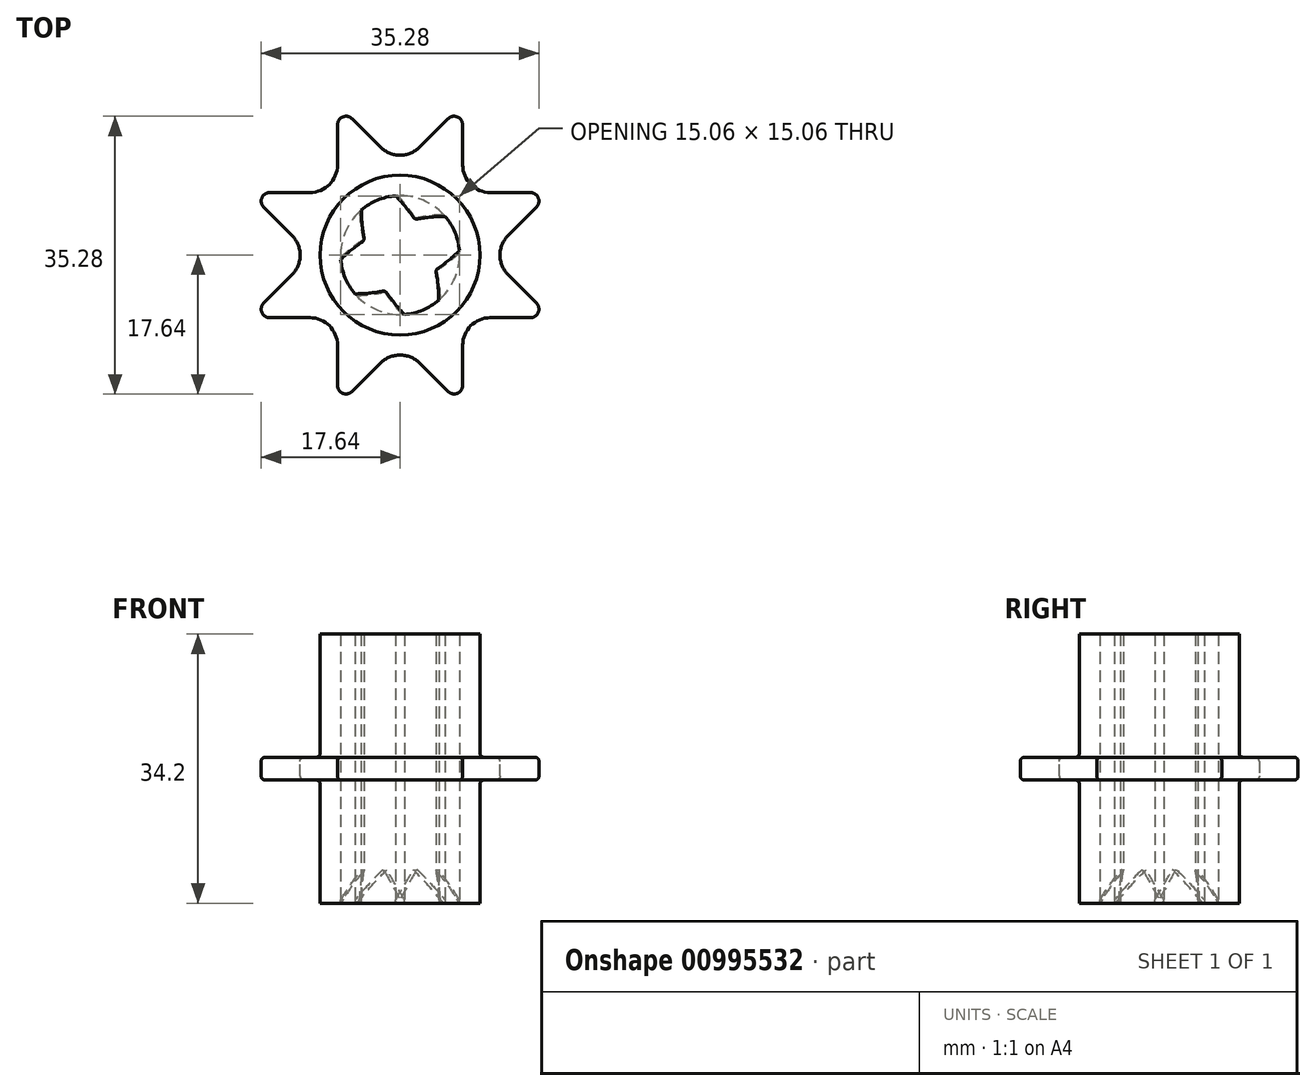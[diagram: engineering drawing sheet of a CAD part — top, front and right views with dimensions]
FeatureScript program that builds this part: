
annotation { "Feature Type Name" : "Feature", "Feature Type Description" : "" }
export const myFeature = defineFeature(function(context is Context, id is Id, definition is map)
    precondition{}
    {
        {
            var Q0;
            Q0=qCreatedBy(makeId("Top.planeOp"),FACE);
            var sketch = newSketch(context, id + "F0", { "sketchPlane" : qUnion([Q0])});
            skCircle(sketch, "E0", {"center": v(0, 0) * mm, "radius": 7.95 * mm, "construction": true});
            skCircle(sketch, "E1", {"center": v(0, 0) * mm, "radius": 20.77 * mm, "construction": true});
            skLineSegment(sketch, "E2", {"start": v(-19.2, 7.95) * mm, "end": v(19.2, 7.95) * mm, "construction": true});
            skLineSegment(sketch, "E3", {"start": v(-19.2, -7.95) * mm, "end": v(19.2, -7.95) * mm, "construction": true});
            skLineSegment(sketch, "E4", {"start": v(-7.95, -19.2) * mm, "end": v(-7.95, 19.2) * mm, "construction": true});
            skLineSegment(sketch, "E5", {"start": v(7.95, 19.2) * mm, "end": v(7.95, -19.2) * mm, "construction": true});
            skLineSegment(sketch, "E6", {"start": v(-19.2, -7.95) * mm, "end": v(7.95, 19.2) * mm, "construction": true});
            skLineSegment(sketch, "E7", {"start": v(-7.95, 19.2) * mm, "end": v(19.2, -7.95) * mm, "construction": true});
            skLineSegment(sketch, "E8", {"start": v(-7.95, -19.2) * mm, "end": v(19.2, 7.95) * mm, "construction": true});
            skLineSegment(sketch, "E9", {"start": v(7.95, -19.2) * mm, "end": v(-19.2, 7.95) * mm, "construction": true});
            skLineSegment(sketch, "E10", {"start": v(-7.95, -19.2) * mm, "end": v(0, -11.24) * mm});
            skLineSegment(sketch, "E11", {"start": v(0, -11.24) * mm, "end": v(7.95, -19.2) * mm});
            skLineSegment(sketch, "E12", {"start": v(7.95, -7.95) * mm, "end": v(7.95, -19.2) * mm});
            skLineSegment(sketch, "E13", {"start": v(19.2, -7.95) * mm, "end": v(7.95, -7.95) * mm});
            skLineSegment(sketch, "E14", {"start": v(11.24, 0) * mm, "end": v(19.2, -7.95) * mm});
            skLineSegment(sketch, "E15", {"start": v(19.2, 7.95) * mm, "end": v(11.24, 0) * mm});
            skLineSegment(sketch, "E16", {"start": v(19.2, 7.95) * mm, "end": v(7.95, 7.95) * mm});
            skLineSegment(sketch, "E17", {"start": v(7.95, 7.95) * mm, "end": v(7.95, 19.2) * mm});
            skLineSegment(sketch, "E18", {"start": v(7.95, 19.2) * mm, "end": v(0, 11.24) * mm});
            skLineSegment(sketch, "E19", {"start": v(-7.95, 19.2) * mm, "end": v(0, 11.24) * mm});
            skLineSegment(sketch, "E20", {"start": v(-7.95, 19.2) * mm, "end": v(-7.95, 7.95) * mm});
            skLineSegment(sketch, "E21", {"start": v(-7.95, 7.95) * mm, "end": v(-19.2, 7.95) * mm});
            skLineSegment(sketch, "E22", {"start": v(-19.2, 7.95) * mm, "end": v(-11.24, 0) * mm});
            skLineSegment(sketch, "E23", {"start": v(-11.24, 0) * mm, "end": v(-19.2, -7.95) * mm});
            skLineSegment(sketch, "E24", {"start": v(-19.2, -7.95) * mm, "end": v(-7.95, -7.95) * mm});
            skLineSegment(sketch, "E25", {"start": v(-7.95, -7.95) * mm, "end": v(-7.95, -19.2) * mm});
            skCircle(sketch, "E26", {"center": v(0, 0) * mm, "radius": 10.15 * mm});
            skSolve(sketch);
        }
        {
            var Q0;
            Q0=makeQuery(id+"F0.imprint","IMPRINT",FACE,{"disambiguationData":[TD([[makeQuery(id+"F0.imprint","IMPRINT",EDGE,{"derivedFrom":sQuery(id+"F0.wireOp",EDGE,"E26")}),1.0]])]});
            extrude(context, id + "F1", {"entities" : qUnion([Q0]), "endBound" : BoundingType.SYMMETRIC, "depth" : 34.2 * mm, "offsetDistance" : 25 * mm});
        }
        {
            var Q0;
            Q0=makeQuery(id+"F0.imprint","IMPRINT",FACE,{"disambiguationData":[TD([[makeQuery(id+"F0.imprint","IMPRINT",EDGE,{"derivedFrom":sQuery(id+"F0.wireOp",EDGE,"E10")}),1.0]])]});
            var Q1;
            Q1=makeQuery(id+"F0.imprint","IMPRINT",FACE,{"disambiguationData":[TD([[makeQuery(id+"F0.imprint","IMPRINT",EDGE,{"derivedFrom":sQuery(id+"F0.wireOp",EDGE,"E26")}),1.0]])]});
            extrude(context, id + "F2", {"entities" : qUnion([Q0, Q1]), "operationType" : NewBodyOperationType.ADD, "endBound" : BoundingType.SYMMETRIC, "depth" : 2.9 * mm, "offsetDistance" : 25 * mm});
        }
        {
            var Q0;
            Q0=makeQuery(id+"F2.opExtrude","SWEPT_EDGE",EDGE,{"disambiguationData":[OSD([sQuery(id+"F0.wireOp",EDGE,"E16"),sQuery(id+"F0.wireOp",EDGE,"E17")])]});
            var Q1;
            Q1=makeQuery(id+"F2.opExtrude","SWEPT_EDGE",EDGE,{"disambiguationData":[OSD([sQuery(id+"F0.wireOp",EDGE,"E18"),sQuery(id+"F0.wireOp",EDGE,"E19")])]});
            var Q2;
            Q2=makeQuery(id+"F2.opExtrude","SWEPT_EDGE",EDGE,{"disambiguationData":[OSD([sQuery(id+"F0.wireOp",EDGE,"E20"),sQuery(id+"F0.wireOp",EDGE,"E21")])]});
            var Q3;
            Q3=makeQuery(id+"F2.opExtrude","SWEPT_EDGE",EDGE,{"disambiguationData":[OSD([sQuery(id+"F0.wireOp",EDGE,"E22"),sQuery(id+"F0.wireOp",EDGE,"E23")])]});
            var Q4;
            Q4=makeQuery(id+"F2.opExtrude","SWEPT_EDGE",EDGE,{"disambiguationData":[OSD([sQuery(id+"F0.wireOp",EDGE,"E24"),sQuery(id+"F0.wireOp",EDGE,"E25")])]});
            var Q5;
            Q5=makeQuery(id+"F2.opExtrude","SWEPT_EDGE",EDGE,{"disambiguationData":[OSD([sQuery(id+"F0.wireOp",EDGE,"E10"),sQuery(id+"F0.wireOp",EDGE,"E11")])]});
            var Q6;
            Q6=makeQuery(id+"F2.opExtrude","SWEPT_EDGE",EDGE,{"disambiguationData":[OSD([sQuery(id+"F0.wireOp",EDGE,"E12"),sQuery(id+"F0.wireOp",EDGE,"E13")])]});
            var Q7;
            Q7=makeQuery(id+"F2.opExtrude","SWEPT_EDGE",EDGE,{"disambiguationData":[OSD([sQuery(id+"F0.wireOp",EDGE,"E14"),sQuery(id+"F0.wireOp",EDGE,"E15")])]});
            fillet(context, id + "F3", {"entities" : qUnion([Q0, Q1, Q2, Q3, Q4, Q5, Q6, Q7]), "radius" : 3.5 * mm, "tangentPropagation" : true, "allowEdgeOverflow" : false});
        }
        {
            var Q0;
            Q0=makeQuery(id+"F2.opExtrude","SWEPT_EDGE",EDGE,{"disambiguationData":[OSD([sQuery(id+"F0.wireOp",EDGE,"E13"),sQuery(id+"F0.wireOp",EDGE,"E14")])]});
            var Q1;
            Q1=makeQuery(id+"F2.opExtrude","SWEPT_EDGE",EDGE,{"disambiguationData":[OSD([sQuery(id+"F0.wireOp",EDGE,"E11"),sQuery(id+"F0.wireOp",EDGE,"E12")])]});
            var Q2;
            Q2=makeQuery(id+"F2.opExtrude","SWEPT_EDGE",EDGE,{"disambiguationData":[OSD([sQuery(id+"F0.wireOp",EDGE,"E10"),sQuery(id+"F0.wireOp",EDGE,"E25")])]});
            var Q3;
            Q3=makeQuery(id+"F2.opExtrude","SWEPT_EDGE",EDGE,{"disambiguationData":[OSD([sQuery(id+"F0.wireOp",EDGE,"E23"),sQuery(id+"F0.wireOp",EDGE,"E24")])]});
            var Q4;
            Q4=makeQuery(id+"F2.opExtrude","SWEPT_EDGE",EDGE,{"disambiguationData":[OSD([sQuery(id+"F0.wireOp",EDGE,"E21"),sQuery(id+"F0.wireOp",EDGE,"E22")])]});
            var Q5;
            Q5=makeQuery(id+"F2.opExtrude","SWEPT_EDGE",EDGE,{"disambiguationData":[OSD([sQuery(id+"F0.wireOp",EDGE,"E19"),sQuery(id+"F0.wireOp",EDGE,"E20")])]});
            var Q6;
            Q6=makeQuery(id+"F2.opExtrude","SWEPT_EDGE",EDGE,{"disambiguationData":[OSD([sQuery(id+"F0.wireOp",EDGE,"E17"),sQuery(id+"F0.wireOp",EDGE,"E18")])]});
            var Q7;
            Q7=makeQuery(id+"F2.opExtrude","SWEPT_EDGE",EDGE,{"disambiguationData":[OSD([sQuery(id+"F0.wireOp",EDGE,"E15"),sQuery(id+"F0.wireOp",EDGE,"E16")])]});
            fillet(context, id + "F4", {"entities" : qUnion([Q0, Q1, Q2, Q3, Q4, Q5, Q6, Q7]), "radius" : 1.1 * mm, "tangentPropagation" : true, "allowEdgeOverflow" : false});
        }
        {
            var Q0;
            Q0=makeQuery(id+"F1.opExtrude","CAP_FACE",FACE,{"disambiguationData":[OSD([sQuery(id+"F0.wireOp",EDGE,"E26")])],"isStart":true});
            var sketch = newSketch(context, id + "F5", { "sketchPlane" : qUnion([Q0])});
            skCircle(sketch, "E27", {"center": v(0, 0) * mm, "radius": 7.55 * mm});
            skCircle(sketch, "E28.0", {"center": v(0, 0) * mm, "radius": 10.15 * mm});
            skArc(sketch, "E29.0", {"start": v(7.95, 16.54) * mm, "mid": v(7.27, 17.55) * mm, "end": v(6.07, 17.32) * mm});
            skArc(sketch, "E29.1", {"start": v(-7.95, -16.54) * mm, "mid": v(-7.27, -17.55) * mm, "end": v(-6.07, -17.32) * mm});
            skLineSegment(sketch, "E30", {"start": v(6.85, 16.54) * mm, "end": v(-6.85, -16.54) * mm, "construction": true});
            skLineSegment(sketch, "E31", {"start": v(-4.92, -5.73) * mm, "end": v(0.57, 7.53) * mm, "construction": true});
            skLineSegment(sketch, "E32", {"start": v(-0.57, -7.53) * mm, "end": v(4.92, 5.73) * mm, "construction": true});
            skLineSegment(sketch, "E33", {"start": v(-7.53, 0.57) * mm, "end": v(5.73, -4.92) * mm, "construction": true});
            skPoint(sketch, "E34.endSnap0", {"position": v(2.18, -0.9) * mm});
            skLineSegment(sketch, "E35", {"start": v(-5.73, 4.92) * mm, "end": v(7.53, -0.57) * mm, "construction": true});
            skLineSegment(sketch, "E36", {"start": v(0, 0) * mm, "end": v(8.18, -3.39) * mm, "construction": true});
            skArc(sketch, "E37", {"start": v(0.57, 7.53) * mm, "mid": v(-3.5, 1.45) * mm, "end": v(-4.92, -5.73) * mm});
            skArc(sketch, "E38", {"start": v(-0.57, -7.53) * mm, "mid": v(3.5, -1.45) * mm, "end": v(4.92, 5.73) * mm});
            skArc(sketch, "E39", {"start": v(7.53, -0.57) * mm, "mid": v(1.45, 3.5) * mm, "end": v(-5.73, 4.92) * mm});
            skArc(sketch, "E40", {"start": v(-7.53, 0.57) * mm, "mid": v(-1.45, -3.5) * mm, "end": v(5.73, -4.92) * mm});
            skPoint(sketch, "E41", {"position": v(1.87, -4.52) * mm});
            skPoint(sketch, "E42", {"position": v(4.52, 1.87) * mm});
            skSolve(sketch);
        }
        {
            var Q0;
            {var subQ0=sQuery(id+"F5.wireOp",EDGE,"E37");var subQ1=sQuery(id+"F5.wireOp",EDGE,"E27");var subQ2=makeQuery(id+"F5.imprint","INTERSECT",VERTEX,{"disambiguationData":[OD(0.0)],"derivedFrom":[subQ1,subQ0]});Q0=makeQuery(id+"F5.imprint","IMPRINT",FACE,{"disambiguationData":[TD([[makeQuery(id+"F5.imprint","IMPRINT",EDGE,{"disambiguationData":[TD([[subQ2,1.0]])],"derivedFrom":subQ1}),1.0]])]});}
            var Q1;
            {var subQ0=sQuery(id+"F5.wireOp",EDGE,"E39");var subQ1=sQuery(id+"F5.wireOp",EDGE,"E37");var subQ2=makeQuery(id+"F5.imprint","INTERSECT",VERTEX,{"derivedFrom":[subQ1,subQ0]});Q1=makeQuery(id+"F5.imprint","IMPRINT",FACE,{"disambiguationData":[TD([[makeQuery(id+"F5.imprint","IMPRINT",EDGE,{"disambiguationData":[TD([[subQ2,-1.0]])],"derivedFrom":subQ1}),1.0]])]});}
            var Q2;
            {var subQ0=sQuery(id+"F5.wireOp",EDGE,"E39");var subQ1=sQuery(id+"F5.wireOp",EDGE,"E27");var subQ2=makeQuery(id+"F5.imprint","INTERSECT",VERTEX,{"disambiguationData":[OD(1.0)],"derivedFrom":[subQ1,subQ0]});Q2=makeQuery(id+"F5.imprint","IMPRINT",FACE,{"disambiguationData":[TD([[makeQuery(id+"F5.imprint","IMPRINT",EDGE,{"disambiguationData":[TD([[subQ2,-1.0]])],"derivedFrom":subQ1}),1.0]])]});}
            var Q3;
            {var subQ0=sQuery(id+"F5.wireOp",EDGE,"E39");var subQ1=sQuery(id+"F5.wireOp",EDGE,"E27");var subQ2=makeQuery(id+"F5.imprint","INTERSECT",VERTEX,{"disambiguationData":[OD(0.0)],"derivedFrom":[subQ1,subQ0]});Q3=makeQuery(id+"F5.imprint","IMPRINT",FACE,{"disambiguationData":[TD([[makeQuery(id+"F5.imprint","IMPRINT",EDGE,{"disambiguationData":[TD([[subQ2,1.0]])],"derivedFrom":subQ1}),1.0]])]});}
            var Q4;
            {var subQ0=sQuery(id+"F5.wireOp",EDGE,"E37");var subQ1=sQuery(id+"F5.wireOp",EDGE,"E27");var subQ2=makeQuery(id+"F5.imprint","INTERSECT",VERTEX,{"disambiguationData":[OD(1.0)],"derivedFrom":[subQ1,subQ0]});Q4=makeQuery(id+"F5.imprint","IMPRINT",FACE,{"disambiguationData":[TD([[makeQuery(id+"F5.imprint","IMPRINT",EDGE,{"disambiguationData":[TD([[subQ2,-1.0]])],"derivedFrom":subQ1}),1.0]])]});}
            extrude(context, id + "F6", {"entities" : qUnion([Q0, Q1, Q2, Q3, Q4]), "operationType" : NewBodyOperationType.REMOVE, "endBound" : BoundingType.THROUGH_ALL, "oppositeDirection" : true, "depth" : 25 * mm, "offsetDistance" : 25 * mm});
        }
        {
            var Q0;
            {var subQ0=sQuery(id+"F5.wireOp",EDGE,"E38");var subQ1=sQuery(id+"F5.wireOp",EDGE,"E27");var subQ2=makeQuery(id+"F5.imprint","INTERSECT",VERTEX,{"disambiguationData":[OD(0.0)],"derivedFrom":[subQ1,subQ0]});Q0=makeQuery(id+"F5.imprint","IMPRINT",FACE,{"disambiguationData":[TD([[makeQuery(id+"F5.imprint","IMPRINT",EDGE,{"disambiguationData":[TD([[subQ2,-1.0]])],"derivedFrom":subQ1}),1.0]])]});}
            var Q1;
            {var subQ0=sQuery(id+"F5.wireOp",EDGE,"E37");var subQ1=sQuery(id+"F5.wireOp",EDGE,"E27");var subQ2=makeQuery(id+"F5.imprint","INTERSECT",VERTEX,{"disambiguationData":[OD(1.0)],"derivedFrom":[subQ1,subQ0]});Q1=makeQuery(id+"F5.imprint","IMPRINT",FACE,{"disambiguationData":[TD([[makeQuery(id+"F5.imprint","IMPRINT",EDGE,{"disambiguationData":[TD([[subQ2,-1.0]])],"derivedFrom":subQ1}),1.0]])]});}
            var Q2;
            {var subQ0=sQuery(id+"F5.wireOp",EDGE,"E37");var subQ1=sQuery(id+"F5.wireOp",EDGE,"E27");var subQ2=makeQuery(id+"F5.imprint","INTERSECT",VERTEX,{"disambiguationData":[OD(0.0)],"derivedFrom":[subQ1,subQ0]});Q2=makeQuery(id+"F5.imprint","IMPRINT",FACE,{"disambiguationData":[TD([[makeQuery(id+"F5.imprint","IMPRINT",EDGE,{"disambiguationData":[TD([[subQ2,-1.0]])],"derivedFrom":subQ1}),1.0]])]});}
            var Q3;
            {var subQ0=sQuery(id+"F5.wireOp",EDGE,"E37");var subQ1=sQuery(id+"F5.wireOp",EDGE,"E27");var subQ2=makeQuery(id+"F5.imprint","INTERSECT",VERTEX,{"disambiguationData":[OD(0.0)],"derivedFrom":[subQ1,subQ0]});Q3=makeQuery(id+"F5.imprint","IMPRINT",FACE,{"disambiguationData":[TD([[makeQuery(id+"F5.imprint","IMPRINT",EDGE,{"disambiguationData":[TD([[subQ2,1.0]])],"derivedFrom":subQ1}),1.0]])]});}
            var Q4;
            {var subQ0=sQuery(id+"F5.wireOp",EDGE,"E37");var subQ1=sQuery(id+"F5.wireOp",EDGE,"E27");var subQ2=makeQuery(id+"F5.imprint","INTERSECT",VERTEX,{"disambiguationData":[OD(1.0)],"derivedFrom":[subQ1,subQ0]});Q4=makeQuery(id+"F5.imprint","IMPRINT",FACE,{"disambiguationData":[TD([[makeQuery(id+"F5.imprint","IMPRINT",EDGE,{"disambiguationData":[TD([[subQ2,1.0]])],"derivedFrom":subQ1}),1.0]])]});}
            var Q5;
            {var subQ0=sQuery(id+"F5.wireOp",EDGE,"E39");var subQ1=sQuery(id+"F5.wireOp",EDGE,"E27");var subQ2=makeQuery(id+"F5.imprint","INTERSECT",VERTEX,{"disambiguationData":[OD(1.0)],"derivedFrom":[subQ1,subQ0]});Q5=makeQuery(id+"F5.imprint","IMPRINT",FACE,{"disambiguationData":[TD([[makeQuery(id+"F5.imprint","IMPRINT",EDGE,{"disambiguationData":[TD([[subQ2,-1.0]])],"derivedFrom":subQ1}),1.0]])]});}
            var Q6;
            {var subQ0=sQuery(id+"F5.wireOp",EDGE,"E39");var subQ1=sQuery(id+"F5.wireOp",EDGE,"E37");var subQ2=makeQuery(id+"F5.imprint","INTERSECT",VERTEX,{"derivedFrom":[subQ1,subQ0]});Q6=makeQuery(id+"F5.imprint","IMPRINT",FACE,{"disambiguationData":[TD([[makeQuery(id+"F5.imprint","IMPRINT",EDGE,{"disambiguationData":[TD([[subQ2,-1.0]])],"derivedFrom":subQ1}),1.0]])]});}
            var Q7;
            {var subQ0=sQuery(id+"F5.wireOp",EDGE,"E38");var subQ1=sQuery(id+"F5.wireOp",EDGE,"E27");var subQ2=makeQuery(id+"F5.imprint","INTERSECT",VERTEX,{"disambiguationData":[OD(1.0)],"derivedFrom":[subQ1,subQ0]});Q7=makeQuery(id+"F5.imprint","IMPRINT",FACE,{"disambiguationData":[TD([[makeQuery(id+"F5.imprint","IMPRINT",EDGE,{"disambiguationData":[TD([[subQ2,1.0]])],"derivedFrom":subQ1}),1.0]])]});}
            var Q8;
            {var subQ0=sQuery(id+"F5.wireOp",EDGE,"E39");var subQ1=sQuery(id+"F5.wireOp",EDGE,"E27");var subQ2=makeQuery(id+"F5.imprint","INTERSECT",VERTEX,{"disambiguationData":[OD(0.0)],"derivedFrom":[subQ1,subQ0]});Q8=makeQuery(id+"F5.imprint","IMPRINT",FACE,{"disambiguationData":[TD([[makeQuery(id+"F5.imprint","IMPRINT",EDGE,{"disambiguationData":[TD([[subQ2,1.0]])],"derivedFrom":subQ1}),1.0]])]});}
            extrude(context, id + "F7", {"entities" : qUnion([Q0, Q1, Q2, Q3, Q4, Q5, Q6, Q7, Q8]), "operationType" : NewBodyOperationType.REMOVE, "oppositeDirection" : true, "depth" : 4.2 * mm, "offsetDistance" : 25 * mm, "hasDraft" : true, "draftAngle" : 32 * degree, "draftPullDirection" : true});
        }
        {
            var Q0;
            Q0=makeQuery(id+"F2.boolean.opBoolean","INTERSECT",EDGE,{"derivedFrom":[makeQuery(id+"F1.opExtrude","SWEPT_FACE",FACE,{"disambiguationData":[OSD([sQuery(id+"F0.wireOp",EDGE,"E26")])]}),makeQuery(id+"F2.opExtrude","CAP_FACE",FACE,{"disambiguationData":[OSD([sQuery(id+"F0.wireOp",EDGE,"E10"),sQuery(id+"F0.wireOp",EDGE,"E11"),sQuery(id+"F0.wireOp",EDGE,"E12"),sQuery(id+"F0.wireOp",EDGE,"E13"),sQuery(id+"F0.wireOp",EDGE,"E14"),sQuery(id+"F0.wireOp",EDGE,"E15"),sQuery(id+"F0.wireOp",EDGE,"E16"),sQuery(id+"F0.wireOp",EDGE,"E17"),sQuery(id+"F0.wireOp",EDGE,"E18"),sQuery(id+"F0.wireOp",EDGE,"E19"),sQuery(id+"F0.wireOp",EDGE,"E20"),sQuery(id+"F0.wireOp",EDGE,"E21"),sQuery(id+"F0.wireOp",EDGE,"E22"),sQuery(id+"F0.wireOp",EDGE,"E23"),sQuery(id+"F0.wireOp",EDGE,"E24"),sQuery(id+"F0.wireOp",EDGE,"E25")])],"isStart":true})]});
            var Q1;
            Q1=makeQuery(id+"F2.boolean.opBoolean","INTERSECT",EDGE,{"derivedFrom":[makeQuery(id+"F1.opExtrude","SWEPT_FACE",FACE,{"disambiguationData":[OSD([sQuery(id+"F0.wireOp",EDGE,"E26")])]}),makeQuery(id+"F2.opExtrude","CAP_FACE",FACE,{"disambiguationData":[OSD([sQuery(id+"F0.wireOp",EDGE,"E10"),sQuery(id+"F0.wireOp",EDGE,"E11"),sQuery(id+"F0.wireOp",EDGE,"E12"),sQuery(id+"F0.wireOp",EDGE,"E13"),sQuery(id+"F0.wireOp",EDGE,"E14"),sQuery(id+"F0.wireOp",EDGE,"E15"),sQuery(id+"F0.wireOp",EDGE,"E16"),sQuery(id+"F0.wireOp",EDGE,"E17"),sQuery(id+"F0.wireOp",EDGE,"E18"),sQuery(id+"F0.wireOp",EDGE,"E19"),sQuery(id+"F0.wireOp",EDGE,"E20"),sQuery(id+"F0.wireOp",EDGE,"E21"),sQuery(id+"F0.wireOp",EDGE,"E22"),sQuery(id+"F0.wireOp",EDGE,"E23"),sQuery(id+"F0.wireOp",EDGE,"E24"),sQuery(id+"F0.wireOp",EDGE,"E25")])],"isStart":false})]});
            var Q2;
            Q2=makeQuery(id+"F2.opExtrude","CAP_EDGE",EDGE,{"disambiguationData":[OSD([sQuery(id+"F0.wireOp",EDGE,"E15")])],"isStart":false});
            var Q3;
            Q3=makeQuery(id+"F2.opExtrude","CAP_EDGE",EDGE,{"disambiguationData":[OSD([sQuery(id+"F0.wireOp",EDGE,"E15")])],"isStart":true});
            var Q4;
            Q4=makeQuery(id+"F6.boolean.opBoolean","COPY",EDGE,{"derivedFrom":makeQuery(id+"F6.opExtrude","SWEPT_EDGE",EDGE,{"disambiguationData":[OSD([sQuery(id+"F5.wireOp",EDGE,"E37"),sQuery(id+"F5.wireOp",EDGE,"E39")])]})});
            var Q5;
            Q5=makeQuery(id+"F6.boolean.opBoolean","COPY",EDGE,{"derivedFrom":makeQuery(id+"F6.opExtrude","SWEPT_EDGE",EDGE,{"disambiguationData":[OSD([sQuery(id+"F5.wireOp",EDGE,"E38"),sQuery(id+"F5.wireOp",EDGE,"E39")])]})});
            var Q6;
            Q6=makeQuery(id+"F6.boolean.opBoolean","COPY",EDGE,{"derivedFrom":makeQuery(id+"F6.opExtrude","SWEPT_EDGE",EDGE,{"disambiguationData":[OSD([sQuery(id+"F5.wireOp",EDGE,"E38"),sQuery(id+"F5.wireOp",EDGE,"E40")])]})});
            var Q7;
            Q7=makeQuery(id+"F6.boolean.opBoolean","COPY",EDGE,{"derivedFrom":makeQuery(id+"F6.opExtrude","SWEPT_EDGE",EDGE,{"disambiguationData":[OSD([sQuery(id+"F5.wireOp",EDGE,"E37"),sQuery(id+"F5.wireOp",EDGE,"E40")])]})});
            var Q8;
            {var subQ0=sQuery(id+"F5.wireOp",EDGE,"E27");var subQ1=sQuery(id+"F5.wireOp",EDGE,"E40");Q8=makeQuery(id+"FDMQOyKi8WlfrRa_1.1.F7.boolean.opBoolean","INTERSECT",EDGE,{"derivedFrom":[makeQuery(id+"F6.boolean.opBoolean","COPY",FACE,{"derivedFrom":makeQuery(id+"F6.opExtrude","SWEPT_FACE",FACE,{"disambiguationData":[OSD([subQ1]),TDD([makeQuery(id+"F5.imprint","IMPRINT",EDGE,{"disambiguationData":[TD([[makeQuery(id+"F5.imprint","INTERSECT",VERTEX,{"disambiguationData":[OD(1.0)],"derivedFrom":[subQ0,subQ1]}),1.0]])],"derivedFrom":subQ1})])]})}),makeQuery(id+"FDMQOyKi8WlfrRa_1.1.F7.opExtrude","SWEPT_FACE",FACE,{"disambiguationData":[OSD([subQ0])]})]});}
            var Q9;
            {var subQ0=sQuery(id+"F5.wireOp",EDGE,"E27");var subQ1=sQuery(id+"F5.wireOp",EDGE,"E38");Q9=makeQuery(id+"FDMQOyKi8WlfrRa_1.1.F7.boolean.opBoolean","INTERSECT",EDGE,{"derivedFrom":[makeQuery(id+"F6.boolean.opBoolean","COPY",FACE,{"derivedFrom":makeQuery(id+"F6.opExtrude","SWEPT_FACE",FACE,{"disambiguationData":[OSD([subQ1]),TDD([makeQuery(id+"F5.imprint","IMPRINT",EDGE,{"disambiguationData":[TD([[makeQuery(id+"F5.imprint","INTERSECT",VERTEX,{"disambiguationData":[OD(0.0)],"derivedFrom":[subQ0,subQ1]}),-1.0]])],"derivedFrom":subQ1})])]})}),makeQuery(id+"FDMQOyKi8WlfrRa_1.1.F7.opExtrude","SWEPT_FACE",FACE,{"disambiguationData":[OSD([subQ0])]})]});}
            var Q10;
            {var subQ0=sQuery(id+"F5.wireOp",EDGE,"E27");var subQ1=sQuery(id+"F5.wireOp",EDGE,"E37");Q10=makeQuery(id+"FDMQOyKi8WlfrRa_1.1.F7.boolean.opBoolean","INTERSECT",EDGE,{"derivedFrom":[makeQuery(id+"F6.boolean.opBoolean","COPY",FACE,{"derivedFrom":makeQuery(id+"F6.opExtrude","SWEPT_FACE",FACE,{"disambiguationData":[OSD([subQ1]),TDD([makeQuery(id+"F5.imprint","IMPRINT",EDGE,{"disambiguationData":[TD([[makeQuery(id+"F5.imprint","INTERSECT",VERTEX,{"disambiguationData":[OD(1.0)],"derivedFrom":[subQ0,subQ1]}),1.0]])],"derivedFrom":subQ1})])]})}),makeQuery(id+"FDMQOyKi8WlfrRa_1.1.F7.opExtrude","SWEPT_FACE",FACE,{"disambiguationData":[OSD([subQ0])]})]});}
            var Q11;
            {var subQ0=sQuery(id+"F5.wireOp",EDGE,"E27");var subQ1=sQuery(id+"F5.wireOp",EDGE,"E40");Q11=makeQuery(id+"FDMQOyKi8WlfrRa_1.1.F7.boolean.opBoolean","INTERSECT",EDGE,{"derivedFrom":[makeQuery(id+"F6.boolean.opBoolean","COPY",FACE,{"derivedFrom":makeQuery(id+"F6.opExtrude","SWEPT_FACE",FACE,{"disambiguationData":[OSD([subQ1]),TDD([makeQuery(id+"F5.imprint","IMPRINT",EDGE,{"disambiguationData":[TD([[makeQuery(id+"F5.imprint","INTERSECT",VERTEX,{"disambiguationData":[OD(0.0)],"derivedFrom":[subQ0,subQ1]}),-1.0]])],"derivedFrom":subQ1})])]})}),makeQuery(id+"FDMQOyKi8WlfrRa_1.1.F7.opExtrude","SWEPT_FACE",FACE,{"disambiguationData":[OSD([subQ0])]})]});}
            var Q12;
            {var subQ0=sQuery(id+"F5.wireOp",EDGE,"E27");var subQ1=sQuery(id+"F5.wireOp",EDGE,"E39");Q12=makeQuery(id+"FDMQOyKi8WlfrRa_1.1.F7.boolean.opBoolean","INTERSECT",EDGE,{"derivedFrom":[makeQuery(id+"F6.boolean.opBoolean","COPY",FACE,{"derivedFrom":makeQuery(id+"F6.opExtrude","SWEPT_FACE",FACE,{"disambiguationData":[OSD([subQ1]),TDD([makeQuery(id+"F5.imprint","IMPRINT",EDGE,{"disambiguationData":[TD([[makeQuery(id+"F5.imprint","INTERSECT",VERTEX,{"disambiguationData":[OD(1.0)],"derivedFrom":[subQ0,subQ1]}),1.0]])],"derivedFrom":subQ1})])]})}),makeQuery(id+"FDMQOyKi8WlfrRa_1.1.F7.opExtrude","SWEPT_FACE",FACE,{"disambiguationData":[OSD([subQ0])]})]});}
            var Q13;
            {var subQ0=sQuery(id+"F5.wireOp",EDGE,"E27");var subQ1=sQuery(id+"F5.wireOp",EDGE,"E37");Q13=makeQuery(id+"FDMQOyKi8WlfrRa_1.1.F7.boolean.opBoolean","INTERSECT",EDGE,{"derivedFrom":[makeQuery(id+"F6.boolean.opBoolean","COPY",FACE,{"derivedFrom":makeQuery(id+"F6.opExtrude","SWEPT_FACE",FACE,{"disambiguationData":[OSD([subQ1]),TDD([makeQuery(id+"F5.imprint","IMPRINT",EDGE,{"disambiguationData":[TD([[makeQuery(id+"F5.imprint","INTERSECT",VERTEX,{"disambiguationData":[OD(0.0)],"derivedFrom":[subQ0,subQ1]}),-1.0]])],"derivedFrom":subQ1})])]})}),makeQuery(id+"FDMQOyKi8WlfrRa_1.1.F7.opExtrude","SWEPT_FACE",FACE,{"disambiguationData":[OSD([subQ0])]})]});}
            var Q14;
            {var subQ0=sQuery(id+"F5.wireOp",EDGE,"E27");var subQ1=sQuery(id+"F5.wireOp",EDGE,"E38");Q14=makeQuery(id+"FDMQOyKi8WlfrRa_1.1.F7.boolean.opBoolean","INTERSECT",EDGE,{"derivedFrom":[makeQuery(id+"F6.boolean.opBoolean","COPY",FACE,{"derivedFrom":makeQuery(id+"F6.opExtrude","SWEPT_FACE",FACE,{"disambiguationData":[OSD([subQ1]),TDD([makeQuery(id+"F5.imprint","IMPRINT",EDGE,{"disambiguationData":[TD([[makeQuery(id+"F5.imprint","INTERSECT",VERTEX,{"disambiguationData":[OD(1.0)],"derivedFrom":[subQ0,subQ1]}),1.0]])],"derivedFrom":subQ1})])]})}),makeQuery(id+"FDMQOyKi8WlfrRa_1.1.F7.opExtrude","SWEPT_FACE",FACE,{"disambiguationData":[OSD([subQ0])]})]});}
            var Q15;
            {var subQ0=sQuery(id+"F5.wireOp",EDGE,"E27");var subQ1=sQuery(id+"F5.wireOp",EDGE,"E39");Q15=makeQuery(id+"FDMQOyKi8WlfrRa_1.1.F7.boolean.opBoolean","INTERSECT",EDGE,{"derivedFrom":[makeQuery(id+"F6.boolean.opBoolean","COPY",FACE,{"derivedFrom":makeQuery(id+"F6.opExtrude","SWEPT_FACE",FACE,{"disambiguationData":[OSD([subQ1]),TDD([makeQuery(id+"F5.imprint","IMPRINT",EDGE,{"disambiguationData":[TD([[makeQuery(id+"F5.imprint","INTERSECT",VERTEX,{"disambiguationData":[OD(0.0)],"derivedFrom":[subQ0,subQ1]}),-1.0]])],"derivedFrom":subQ1})])]})}),makeQuery(id+"FDMQOyKi8WlfrRa_1.1.F7.opExtrude","SWEPT_FACE",FACE,{"disambiguationData":[OSD([subQ0])]})]});}
            var Q16;
            {var subQ0=sQuery(id+"F5.wireOp",EDGE,"E27");var subQ1=sQuery(id+"F5.wireOp",EDGE,"E37");Q16=makeQuery(id+"F7.boolean.opBoolean","INTERSECT",EDGE,{"derivedFrom":[makeQuery(id+"F6.boolean.opBoolean","COPY",FACE,{"derivedFrom":makeQuery(id+"F6.opExtrude","SWEPT_FACE",FACE,{"disambiguationData":[OSD([subQ1]),TDD([makeQuery(id+"F5.imprint","IMPRINT",EDGE,{"disambiguationData":[TD([[makeQuery(id+"F5.imprint","INTERSECT",VERTEX,{"disambiguationData":[OD(0.0)],"derivedFrom":[subQ0,subQ1]}),-1.0]])],"derivedFrom":subQ1})])]})}),makeQuery(id+"F7.opExtrude","SWEPT_FACE",FACE,{"disambiguationData":[OSD([subQ0])]})]});}
            var Q17;
            {var subQ0=sQuery(id+"F5.wireOp",EDGE,"E27");var subQ1=sQuery(id+"F5.wireOp",EDGE,"E39");Q17=makeQuery(id+"F7.boolean.opBoolean","INTERSECT",EDGE,{"derivedFrom":[makeQuery(id+"F6.boolean.opBoolean","COPY",FACE,{"derivedFrom":makeQuery(id+"F6.opExtrude","SWEPT_FACE",FACE,{"disambiguationData":[OSD([subQ1]),TDD([makeQuery(id+"F5.imprint","IMPRINT",EDGE,{"disambiguationData":[TD([[makeQuery(id+"F5.imprint","INTERSECT",VERTEX,{"disambiguationData":[OD(1.0)],"derivedFrom":[subQ0,subQ1]}),1.0]])],"derivedFrom":subQ1})])]})}),makeQuery(id+"F7.opExtrude","SWEPT_FACE",FACE,{"disambiguationData":[OSD([subQ0])]})]});}
            var Q18;
            {var subQ0=sQuery(id+"F5.wireOp",EDGE,"E27");var subQ1=sQuery(id+"F5.wireOp",EDGE,"E40");Q18=makeQuery(id+"F7.boolean.opBoolean","INTERSECT",EDGE,{"derivedFrom":[makeQuery(id+"F6.boolean.opBoolean","COPY",FACE,{"derivedFrom":makeQuery(id+"F6.opExtrude","SWEPT_FACE",FACE,{"disambiguationData":[OSD([subQ1]),TDD([makeQuery(id+"F5.imprint","IMPRINT",EDGE,{"disambiguationData":[TD([[makeQuery(id+"F5.imprint","INTERSECT",VERTEX,{"disambiguationData":[OD(0.0)],"derivedFrom":[subQ0,subQ1]}),-1.0]])],"derivedFrom":subQ1})])]})}),makeQuery(id+"F7.opExtrude","SWEPT_FACE",FACE,{"disambiguationData":[OSD([subQ0])]})]});}
            var Q19;
            {var subQ0=sQuery(id+"F5.wireOp",EDGE,"E27");var subQ1=sQuery(id+"F5.wireOp",EDGE,"E37");Q19=makeQuery(id+"F7.boolean.opBoolean","INTERSECT",EDGE,{"derivedFrom":[makeQuery(id+"F6.boolean.opBoolean","COPY",FACE,{"derivedFrom":makeQuery(id+"F6.opExtrude","SWEPT_FACE",FACE,{"disambiguationData":[OSD([subQ1]),TDD([makeQuery(id+"F5.imprint","IMPRINT",EDGE,{"disambiguationData":[TD([[makeQuery(id+"F5.imprint","INTERSECT",VERTEX,{"disambiguationData":[OD(1.0)],"derivedFrom":[subQ0,subQ1]}),1.0]])],"derivedFrom":subQ1})])]})}),makeQuery(id+"F7.opExtrude","SWEPT_FACE",FACE,{"disambiguationData":[OSD([subQ0])]})]});}
            var Q20;
            {var subQ0=sQuery(id+"F5.wireOp",EDGE,"E27");var subQ1=sQuery(id+"F5.wireOp",EDGE,"E38");Q20=makeQuery(id+"F7.boolean.opBoolean","INTERSECT",EDGE,{"derivedFrom":[makeQuery(id+"F6.boolean.opBoolean","COPY",FACE,{"derivedFrom":makeQuery(id+"F6.opExtrude","SWEPT_FACE",FACE,{"disambiguationData":[OSD([subQ1]),TDD([makeQuery(id+"F5.imprint","IMPRINT",EDGE,{"disambiguationData":[TD([[makeQuery(id+"F5.imprint","INTERSECT",VERTEX,{"disambiguationData":[OD(0.0)],"derivedFrom":[subQ0,subQ1]}),-1.0]])],"derivedFrom":subQ1})])]})}),makeQuery(id+"F7.opExtrude","SWEPT_FACE",FACE,{"disambiguationData":[OSD([subQ0])]})]});}
            var Q21;
            {var subQ0=sQuery(id+"F5.wireOp",EDGE,"E27");var subQ1=sQuery(id+"F5.wireOp",EDGE,"E40");Q21=makeQuery(id+"F7.boolean.opBoolean","INTERSECT",EDGE,{"derivedFrom":[makeQuery(id+"F6.boolean.opBoolean","COPY",FACE,{"derivedFrom":makeQuery(id+"F6.opExtrude","SWEPT_FACE",FACE,{"disambiguationData":[OSD([subQ1]),TDD([makeQuery(id+"F5.imprint","IMPRINT",EDGE,{"disambiguationData":[TD([[makeQuery(id+"F5.imprint","INTERSECT",VERTEX,{"disambiguationData":[OD(1.0)],"derivedFrom":[subQ0,subQ1]}),1.0]])],"derivedFrom":subQ1})])]})}),makeQuery(id+"F7.opExtrude","SWEPT_FACE",FACE,{"disambiguationData":[OSD([subQ0])]})]});}
            var Q22;
            {var subQ0=sQuery(id+"F5.wireOp",EDGE,"E27");var subQ1=sQuery(id+"F5.wireOp",EDGE,"E39");Q22=makeQuery(id+"F7.boolean.opBoolean","INTERSECT",EDGE,{"derivedFrom":[makeQuery(id+"F6.boolean.opBoolean","COPY",FACE,{"derivedFrom":makeQuery(id+"F6.opExtrude","SWEPT_FACE",FACE,{"disambiguationData":[OSD([subQ1]),TDD([makeQuery(id+"F5.imprint","IMPRINT",EDGE,{"disambiguationData":[TD([[makeQuery(id+"F5.imprint","INTERSECT",VERTEX,{"disambiguationData":[OD(0.0)],"derivedFrom":[subQ0,subQ1]}),-1.0]])],"derivedFrom":subQ1})])]})}),makeQuery(id+"F7.opExtrude","SWEPT_FACE",FACE,{"disambiguationData":[OSD([subQ0])]})]});}
            var Q23;
            {var subQ0=sQuery(id+"F5.wireOp",EDGE,"E27");var subQ1=sQuery(id+"F5.wireOp",EDGE,"E38");Q23=makeQuery(id+"F7.boolean.opBoolean","INTERSECT",EDGE,{"derivedFrom":[makeQuery(id+"F6.boolean.opBoolean","COPY",FACE,{"derivedFrom":makeQuery(id+"F6.opExtrude","SWEPT_FACE",FACE,{"disambiguationData":[OSD([subQ1]),TDD([makeQuery(id+"F5.imprint","IMPRINT",EDGE,{"disambiguationData":[TD([[makeQuery(id+"F5.imprint","INTERSECT",VERTEX,{"disambiguationData":[OD(1.0)],"derivedFrom":[subQ0,subQ1]}),1.0]])],"derivedFrom":subQ1})])]})}),makeQuery(id+"F7.opExtrude","SWEPT_FACE",FACE,{"disambiguationData":[OSD([subQ0])]})]});}
            fillet(context, id + "F8", {"entities" : qUnion([Q0, Q1, Q2, Q3, Q4, Q5, Q6, Q7, Q8, Q9, Q10, Q11, Q12, Q13, Q14, Q15, Q16, Q17, Q18, Q19, Q20, Q21, Q22, Q23]), "radius" : 0.5 * mm, "tangentPropagation" : true, "allowEdgeOverflow" : false});
        }
    });
